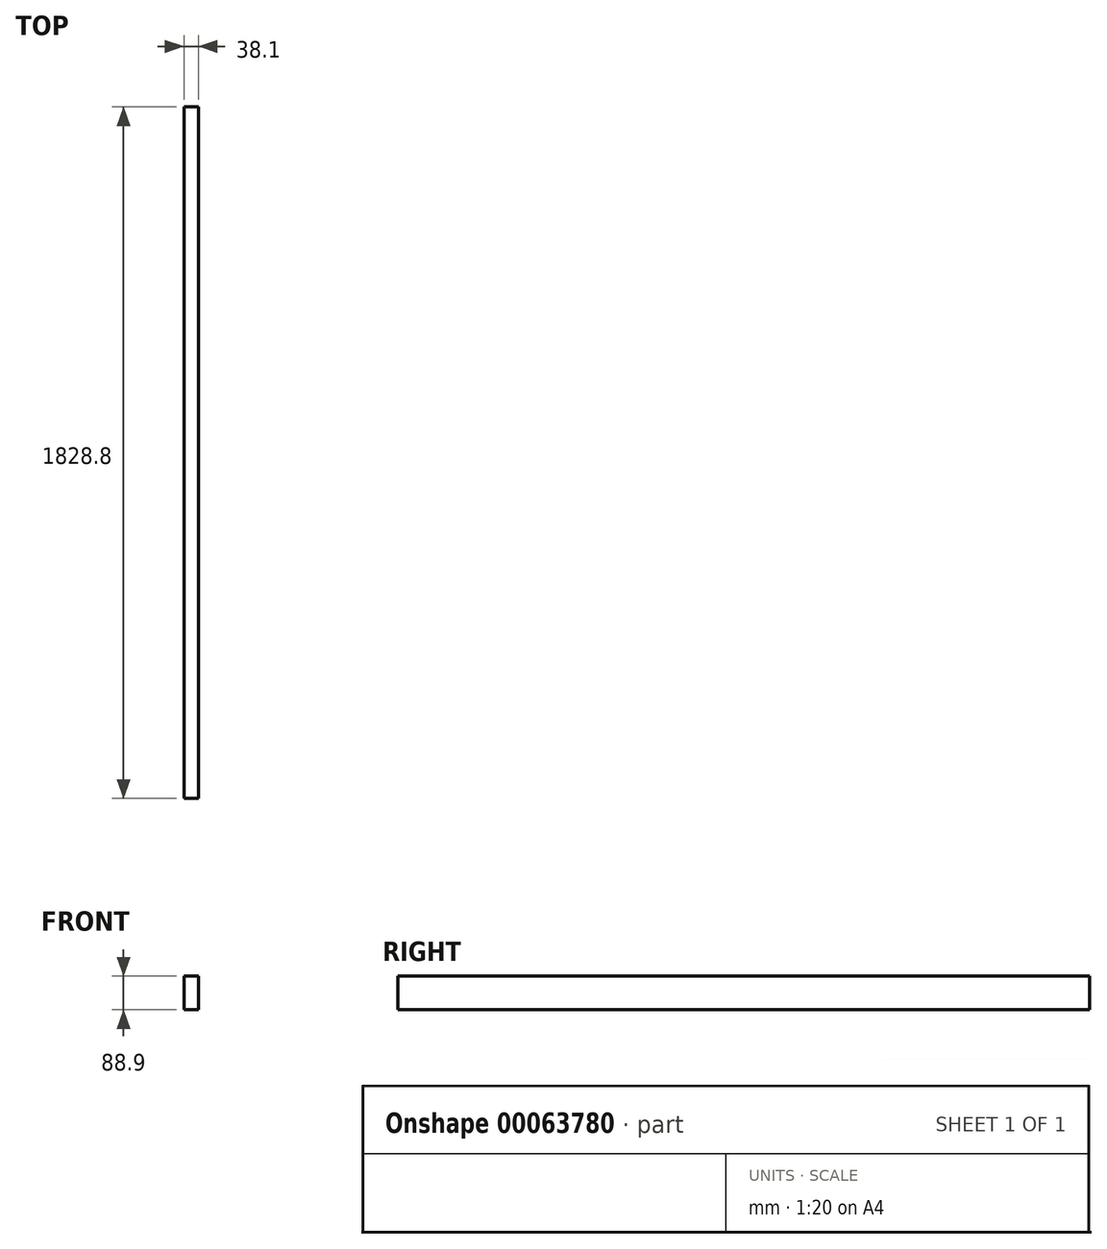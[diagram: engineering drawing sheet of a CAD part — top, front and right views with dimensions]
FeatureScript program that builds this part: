
annotation { "Feature Type Name" : "Feature", "Feature Type Description" : "" }
export const myFeature = defineFeature(function(context is Context, id is Id, definition is map)
    precondition{}
    {
        {
            var Q0;
            Q0=qCreatedBy(makeId("Front.planeOp"),FACE);
            var sketch = newSketch(context, id + "F0", { "sketchPlane" : qUnion([Q0])});
            skLineSegment(sketch, "E0.bottom", {"start": v(-18, 55.77) * mm, "end": v(20.1, 55.77) * mm});
            skLineSegment(sketch, "E0.top", {"start": v(-18, -33.13) * mm, "end": v(20.1, -33.13) * mm});
            skLineSegment(sketch, "E0.left", {"start": v(-18, 55.77) * mm, "end": v(-18, -33.13) * mm});
            skLineSegment(sketch, "E0.right", {"start": v(20.1, 55.77) * mm, "end": v(20.1, -33.13) * mm});
            skSolve(sketch);
        }
        {
            var Q0;
            Q0=qSketchRegion(id+"F0",true);
            extrude(context, id + "F1", {"entities" : qUnion([Q0]), "endBound" : BoundingType.SYMMETRIC, "depth" : 1828.8 * mm});
        }
    });
